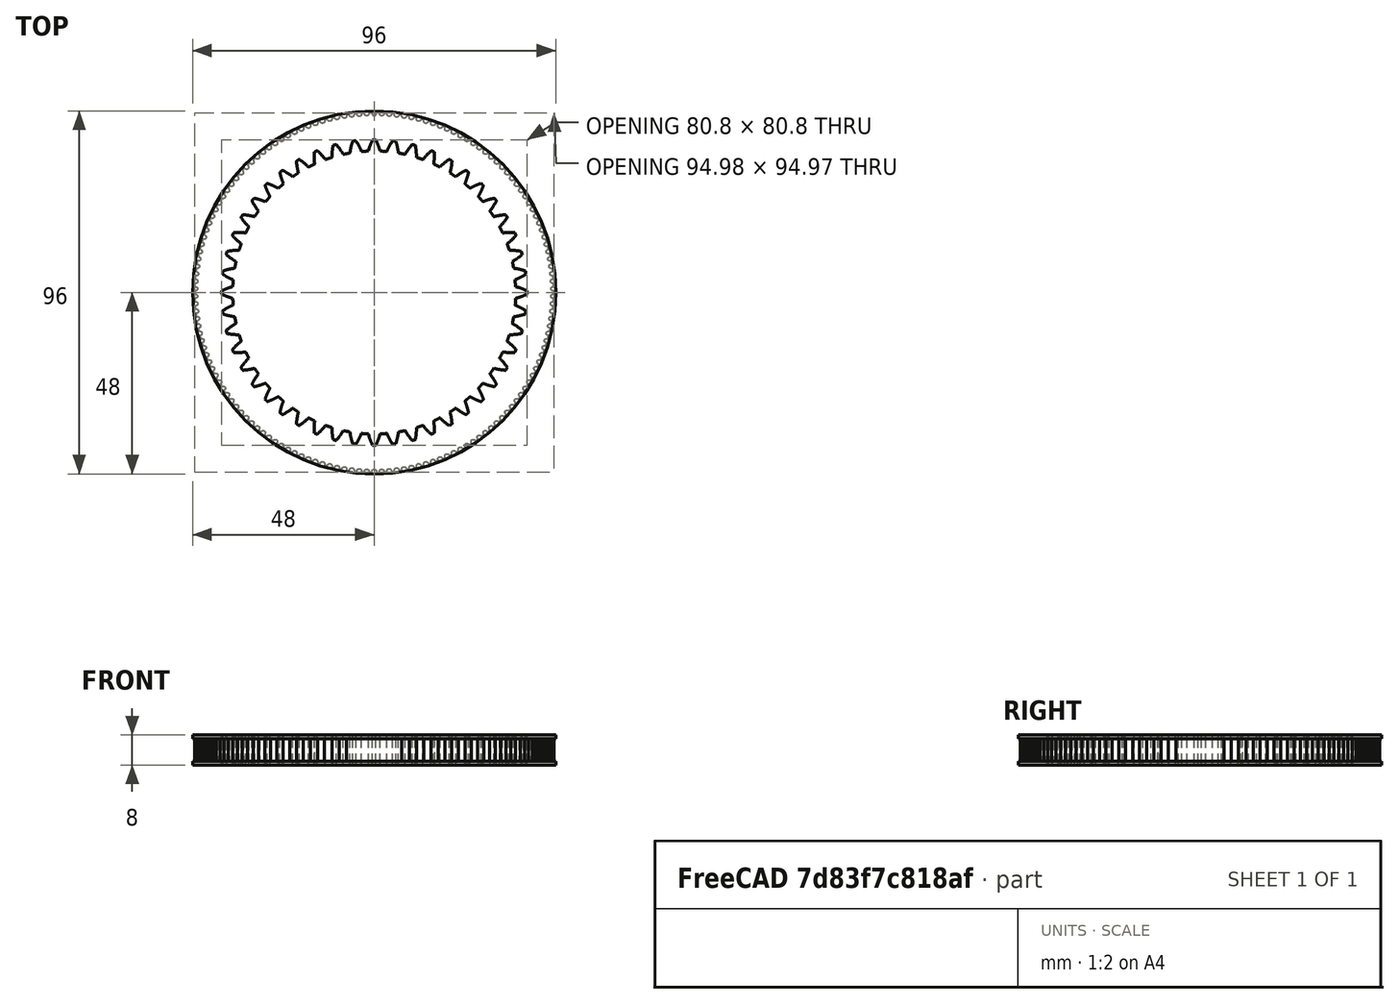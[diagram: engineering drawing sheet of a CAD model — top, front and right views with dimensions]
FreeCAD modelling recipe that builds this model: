
FCSTD DOCUMENT  (FreeCAD 0.20R29603 (Git))
Label: sun_gear_gt2
License: All rights reserved
LicenseURL: http://en.wikipedia.org/wiki/All_rights_reserved
objects: Part::FeaturePython×2, Part::Cylinder×2, Part::Cut×2, Part::MultiCommon×1
note: 7 computed .brp shape members not serialized (recipe doc carries the construction recipe); baked Part::Feature solids carry a one-line shape summary decoded from their .brp

FEATURE [Part::FeaturePython] TimingGear  # WARN: FeaturePython — macro-defined, semantics opaque (R4)
  AttacherType = Attacher::AttachEngine3D
  h = 0.75
  height = 6
  offset = 0.4
  pitch = 2
  r0 = 0.555
  r1 = 1
  rs = 0.15
  teeth = 150
  type = 0
  u = 0.254
  version = 0.0.4
FEATURE [Part::Cylinder] Cylinder
  Angle = 360
  AttacherType = Attacher::AttachEngine3D
  FirstAngle = 0
  Height = 6
  Radius = 48
  SecondAngle = 0
FEATURE [Part::Cut] Cut
  Base = -> Cylinder
  Tool = -> TimingGear
FEATURE [Part::Cylinder] Cylinder001
  Angle = 360
  AttacherType = Attacher::AttachEngine3D
  FirstAngle = 0
  Height = 8
  Placement = pos=(0,0,-1) rot=(0,0,1;0rad)
  Radius = 48
  SecondAngle = 0
FEATURE [Part::Cut] Cut001
  Base = -> Cylinder001
  Tool = -> Cut
FEATURE [Part::FeaturePython] InternalInvoluteGear  # WARN: FeaturePython — macro-defined, semantics opaque (R4)
  AttacherType = Attacher::AttachEngine3D
  Placement = pos=(0,0,-1) rot=(0,0,1;0rad)
  angular_backlash = 0
  backlash = 0
  beta = 0
  clearance = 0.25
  da = 74.88
  df = 80.8
  double_helix = false
  dw = 76.8
  head = -0.4
  head_fillet = 0
  height = 8
  module = 1.6
  numpoints = 6
  outside_diameter = 96.8
  pressure_angle = 20
  properties_from_tool = false
  reversed_backlash = false
  root_fillet = 0
  shift = 0
  simple = false
  teeth = 48
  thickness = 10
  transverse_pitch = 5.02655
  version = 0.0.4
  expr: angular_backlash = backlash / dw * 360° / pi
FEATURE [Part::MultiCommon] Common
  Shapes = -> [Cut001,InternalInvoluteGear]
